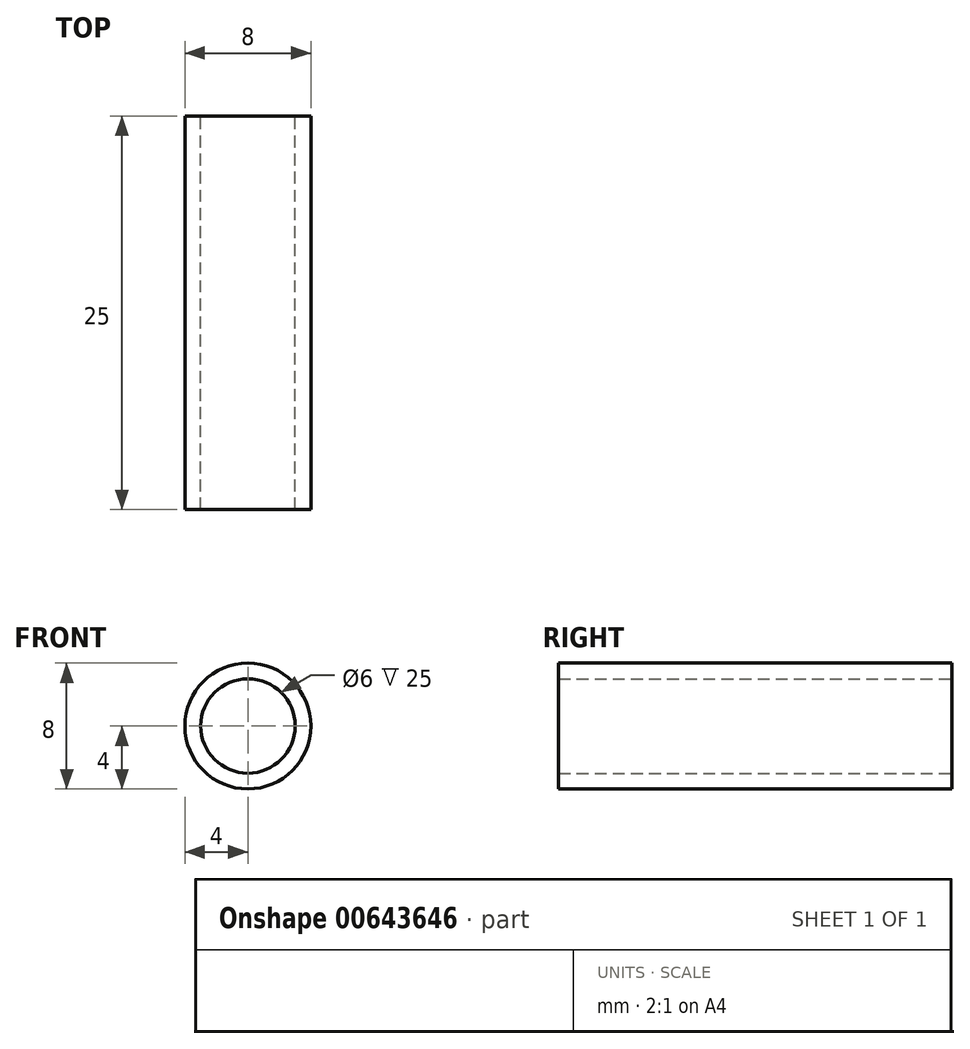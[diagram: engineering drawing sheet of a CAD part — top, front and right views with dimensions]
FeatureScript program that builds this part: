
annotation { "Feature Type Name" : "Feature", "Feature Type Description" : "" }
export const myFeature = defineFeature(function(context is Context, id is Id, definition is map)
    precondition{}
    {
        {
            var Q0;
            Q0=qCreatedBy(makeId("Front.planeOp"),FACE);
            var sketch = newSketch(context, id + "F0", { "sketchPlane" : qUnion([Q0])});
            skCircle(sketch, "E0", {"center": v(0, 0) * mm, "radius": 3 * mm});
            skCircle(sketch, "E1", {"center": v(0, 0) * mm, "radius": 4 * mm});
            skSolve(sketch);
        }
        {
            var Q0;
            Q0 = qSketchRegion(id + "F0", true);
            extrude(context, id + "F1", {"entities" : qUnion([Q0]), "depth" : 25 * mm, "offsetDistance" : 25 * mm});
        }
    });
